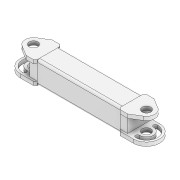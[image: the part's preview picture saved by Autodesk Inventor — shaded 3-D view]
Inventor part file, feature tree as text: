
AUTODESK INVENTOR PART (.ipt)
format: ipt  version: 2020 (Build 240168000, 168)  size: 193,024 bytes
history: mixed  units: mm
features: extrude x6, other x3, sketch x1, imported_body x1
ambient origin geometry x8: Origin, YZ Plane, XZ Plane, XY Plane, X Axis, Y Axis, Z Axis, Center Point
bodies: Solide1 (imported_parasolid), Solide2 (imported_parasolid), Solide3 (imported_parasolid), Solide4 (imported_parasolid), Solide5 (imported_parasolid), Solide6 (imported_parasolid), Solide7 (imported_parasolid), Solide8 (imported_parasolid)
feature tree (11):
  extrude  "Extrusion1"  Depth=52.5mm TaperAngle=0.0deg
  sketch  "Esquisse2"
  other  "Elément mécano-soudé1"
  extrude  "Extrusion2"  Depth=0.5mm
  extrude  "Extrusion4"  Depth=0.872665mm
  other  "Symétrie2[1]"
  other  "Symétrie2[2]"
  extrude  "Extrusion8[1]"  [1 undecoded]
  extrude  "Extrusion8[2]"  [1 undecoded]
  extrude  "Extrusion9"  [1 undecoded]
  imported_body  NMx_Import_Brep_tag  [imported B-rep: ~78 faces, bbox_mm=[322.995884, 60.0, 70.0]]
note: 3 required parameter values undecoded (feature->parameter linkage not recoverable at this tier; creation-order binding heuristic only, values carry confidence <= 0.55)
